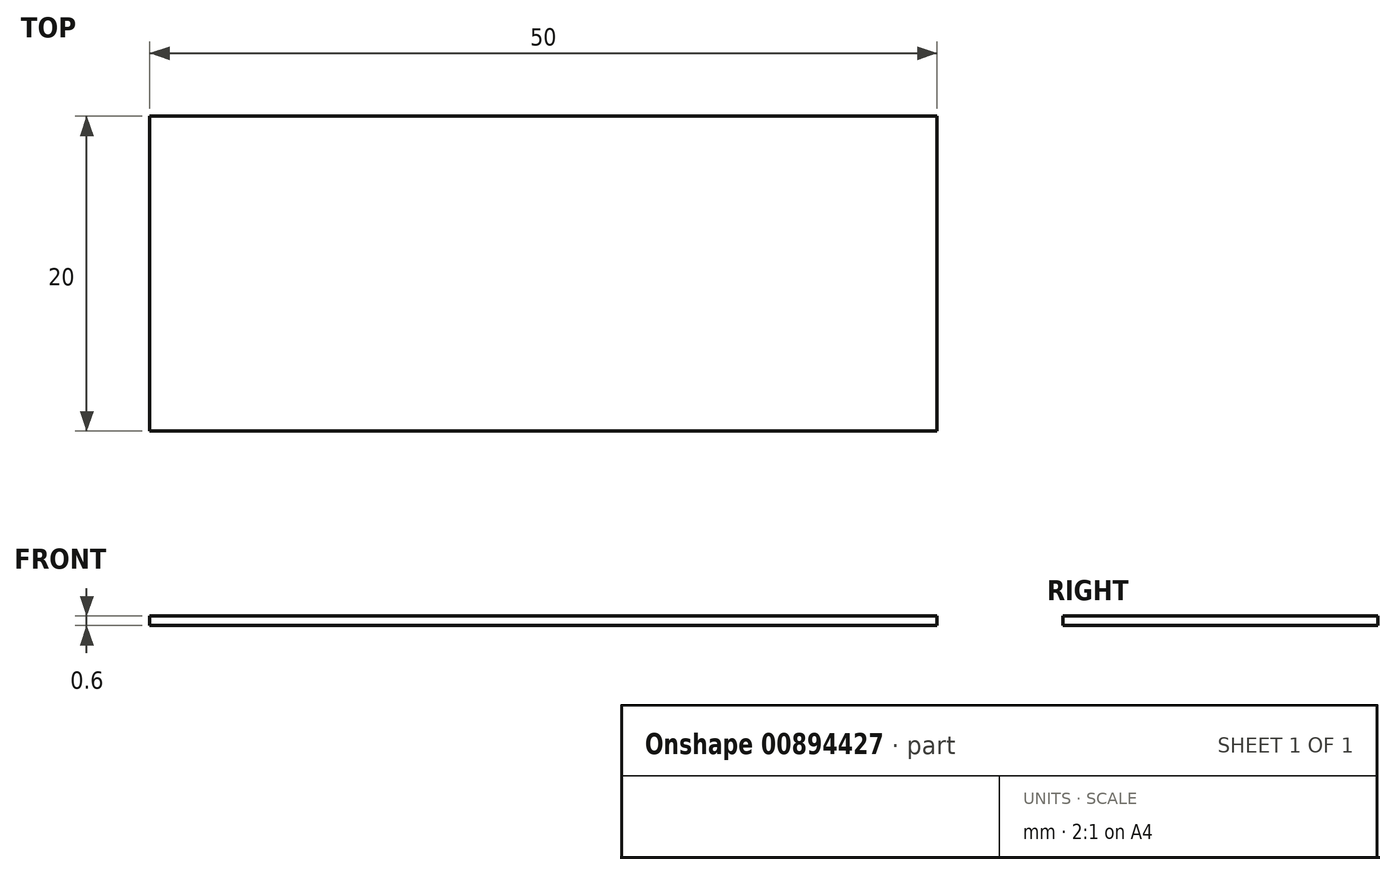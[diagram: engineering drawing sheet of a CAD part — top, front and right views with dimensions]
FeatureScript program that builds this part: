
annotation { "Feature Type Name" : "Feature", "Feature Type Description" : "" }
export const myFeature = defineFeature(function(context is Context, id is Id, definition is map)
    precondition{}
    {
        {
            var Q0;
            Q0=qCreatedBy(makeId("Top.planeOp"),FACE);
            var sketch = newSketch(context, id + "F0", { "sketchPlane" : qUnion([Q0])});
            skLineSegment(sketch, "E0.bottom", {"start": v(25, -10) * mm, "end": v(-25, -10) * mm});
            skLineSegment(sketch, "E0.top", {"start": v(25, 10) * mm, "end": v(-25, 10) * mm});
            skLineSegment(sketch, "E0.left", {"start": v(25, -10) * mm, "end": v(25, 10) * mm});
            skLineSegment(sketch, "E0.right", {"start": v(-25, -10) * mm, "end": v(-25, 10) * mm});
            skPoint(sketch, "E0.middle", {"position": v(0, 0) * mm});
            skSolve(sketch);
        }
        {
            var Q0;
            Q0=makeQuery(id+"F0.imprint","IMPRINT",FACE,{"disambiguationData":[TD([[makeQuery(id+"F0.imprint","IMPRINT",EDGE,{"derivedFrom":sQuery(id+"F0.wireOp",EDGE,"E0.bottom")}),-1.0]])]});
            extrude(context, id + "F1", {"entities" : qUnion([Q0]), "depth" : .6 * mm, "offsetDistance" : 25 * mm});
        }
    });
